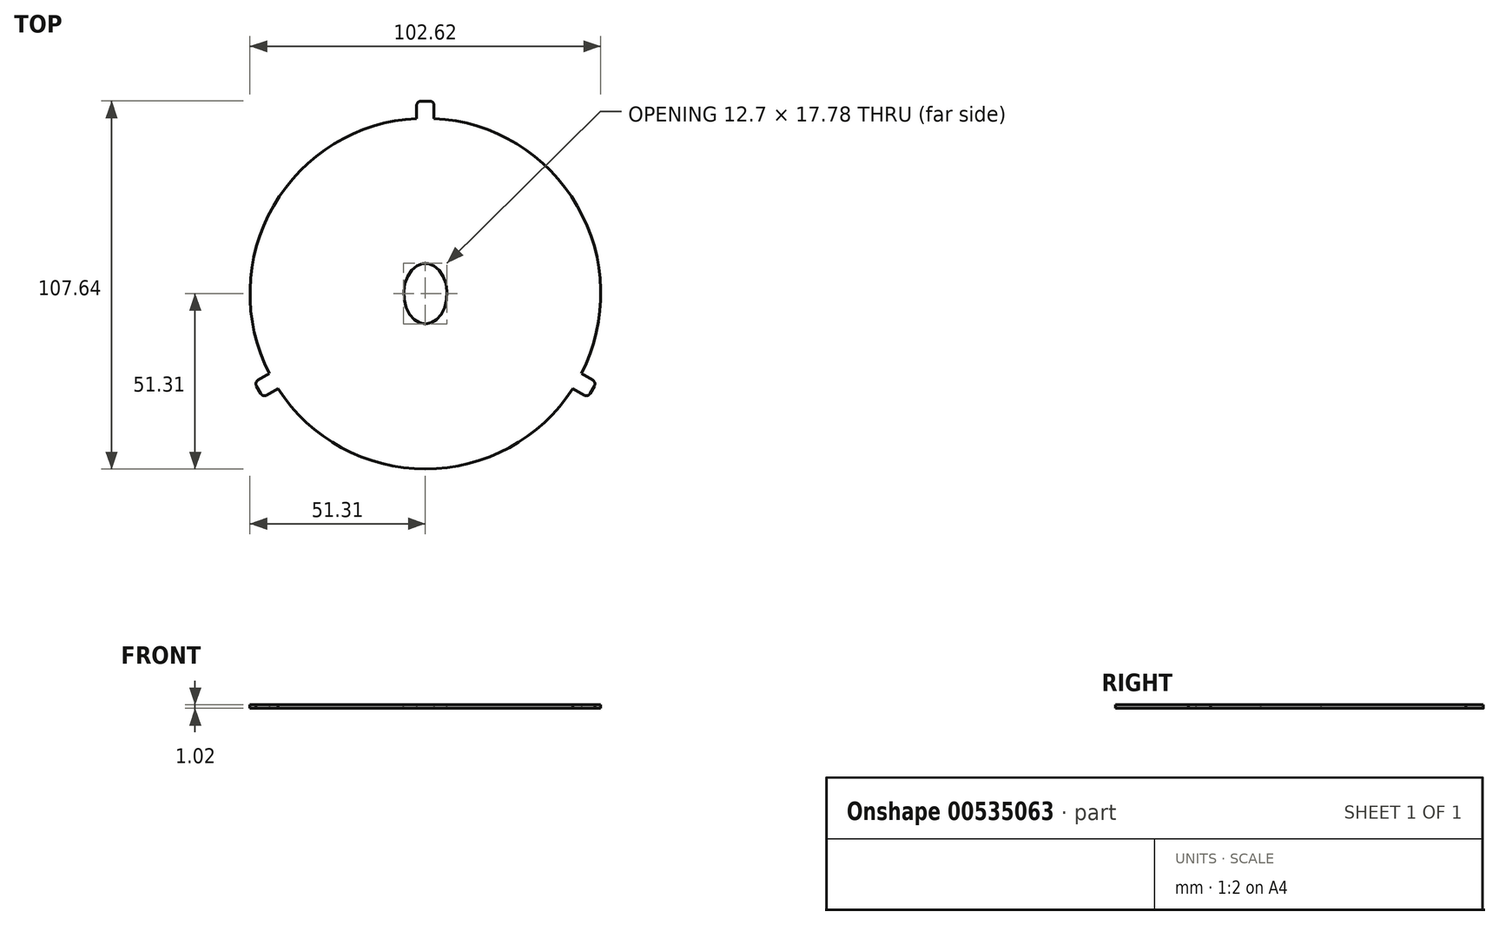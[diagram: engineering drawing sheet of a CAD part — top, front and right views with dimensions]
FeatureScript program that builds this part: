
annotation { "Feature Type Name" : "Feature", "Feature Type Description" : "" }
export const myFeature = defineFeature(function(context is Context, id is Id, definition is map)
    precondition{}
    {
        {
            var Q0;
            Q0=qCreatedBy(makeId("Top.planeOp"),FACE);
            var sketch = newSketch(context, id + "F0", { "sketchPlane" : qUnion([Q0])});
            skCircle(sketch, "E0", {"center": v(0, 0) * mm, "radius": 51.3 * mm});
            skLineSegment(sketch, "E1.bottom", {"start": v(2.54, 51.25) * mm, "end": v(-2.54, 51.25) * mm});
            skLineSegment(sketch, "E1.top", {"start": v(2.54, 56.33) * mm, "end": v(-2.54, 56.33) * mm});
            skLineSegment(sketch, "E1.left", {"start": v(2.54, 51.25) * mm, "end": v(2.54, 56.33) * mm});
            skLineSegment(sketch, "E1.right", {"start": v(-2.54, 51.25) * mm, "end": v(-2.54, 56.33) * mm});
            skPoint(sketch, "E1.middle", {"position": v(0, 53.79) * mm});
            skPoint(sketch, "E2.1.0", {"position": v(-46.58, -26.9) * mm});
            skLineSegment(sketch, "E2.1.1", {"start": v(-43.1, -27.82) * mm, "end": v(-47.5, -30.36) * mm});
            skLineSegment(sketch, "E2.1.2", {"start": v(-45.65, -23.42) * mm, "end": v(-50.05, -25.96) * mm});
            skLineSegment(sketch, "E2.1.3", {"start": v(-50.05, -25.96) * mm, "end": v(-47.5, -30.36) * mm});
            skLineSegment(sketch, "E2.1.4", {"start": v(-45.65, -23.42) * mm, "end": v(-43.1, -27.82) * mm});
            skPoint(sketch, "E2.2.0", {"position": v(46.58, -26.9) * mm});
            skLineSegment(sketch, "E2.2.1", {"start": v(45.65, -23.42) * mm, "end": v(50.05, -25.96) * mm});
            skLineSegment(sketch, "E2.2.2", {"start": v(43.1, -27.82) * mm, "end": v(47.5, -30.36) * mm});
            skLineSegment(sketch, "E2.2.3", {"start": v(47.5, -30.36) * mm, "end": v(50.05, -25.96) * mm});
            skLineSegment(sketch, "E2.2.4", {"start": v(43.1, -27.82) * mm, "end": v(45.65, -23.42) * mm});
            skEllipse(sketch, "E3", {"center": v(0, 0) * mm, "majorRadius": 8.9 * mm, "minorRadius": 6.35 * mm, "majorAxis": v(0, -1)});
            skSolve(sketch);
        }
        {
            var Q0;
            Q0 = qSketchRegion(id + "F0", true);
            extrude(context, id + "F1", {"entities" : qUnion([Q0]), "depth" : 2.03 * mm, "offsetDistance" : 25.4 * mm, "symmetric" : true});
        }
        {
            var Q0;
            Q0 = qSketchRegion(id + "F0", true);
            extrude(context, id + "F2", {"entities" : qUnion([Q0]), "operationType" : NewBodyOperationType.REMOVE, "endBound" : BoundingType.THROUGH_ALL, "oppositeDirection" : true, "depth" : 25.4 * mm, "offsetDistance" : 25.4 * mm});
        }
        {
            var Q0;
            Q0=makeQuery(id+"F1.opExtrude","SWEPT_EDGE",EDGE,{"disambiguationData":[OSD([sQuery(id+"F0.wireOp",EDGE,"E2.1.2"),sQuery(id+"F0.wireOp",EDGE,"E2.1.3")])]});
            var Q1;
            Q1=makeQuery(id+"F1.opExtrude","SWEPT_EDGE",EDGE,{"disambiguationData":[OSD([sQuery(id+"F0.wireOp",EDGE,"E2.1.1"),sQuery(id+"F0.wireOp",EDGE,"E2.1.3")])]});
            var Q2;
            Q2=makeQuery(id+"F1.opExtrude","SWEPT_EDGE",EDGE,{"disambiguationData":[OSD([sQuery(id+"F0.wireOp",EDGE,"E1.top"),sQuery(id+"F0.wireOp",EDGE,"E1.left")])]});
            var Q3;
            Q3=makeQuery(id+"F1.opExtrude","SWEPT_EDGE",EDGE,{"disambiguationData":[OSD([sQuery(id+"F0.wireOp",EDGE,"E1.top"),sQuery(id+"F0.wireOp",EDGE,"E1.right")])]});
            var Q4;
            Q4=makeQuery(id+"F1.opExtrude","SWEPT_EDGE",EDGE,{"disambiguationData":[OSD([sQuery(id+"F0.wireOp",EDGE,"E2.2.1"),sQuery(id+"F0.wireOp",EDGE,"E2.2.3")])]});
            var Q5;
            Q5=makeQuery(id+"F1.opExtrude","SWEPT_EDGE",EDGE,{"disambiguationData":[OSD([sQuery(id+"F0.wireOp",EDGE,"E2.2.2"),sQuery(id+"F0.wireOp",EDGE,"E2.2.3")])]});
            fillet(context, id + "F3", {"entities" : qUnion([Q0, Q1, Q2, Q3, Q4, Q5]), "radius" : 1.27 * mm, "tangentPropagation" : true, "allowEdgeOverflow" : false});
        }
    });
